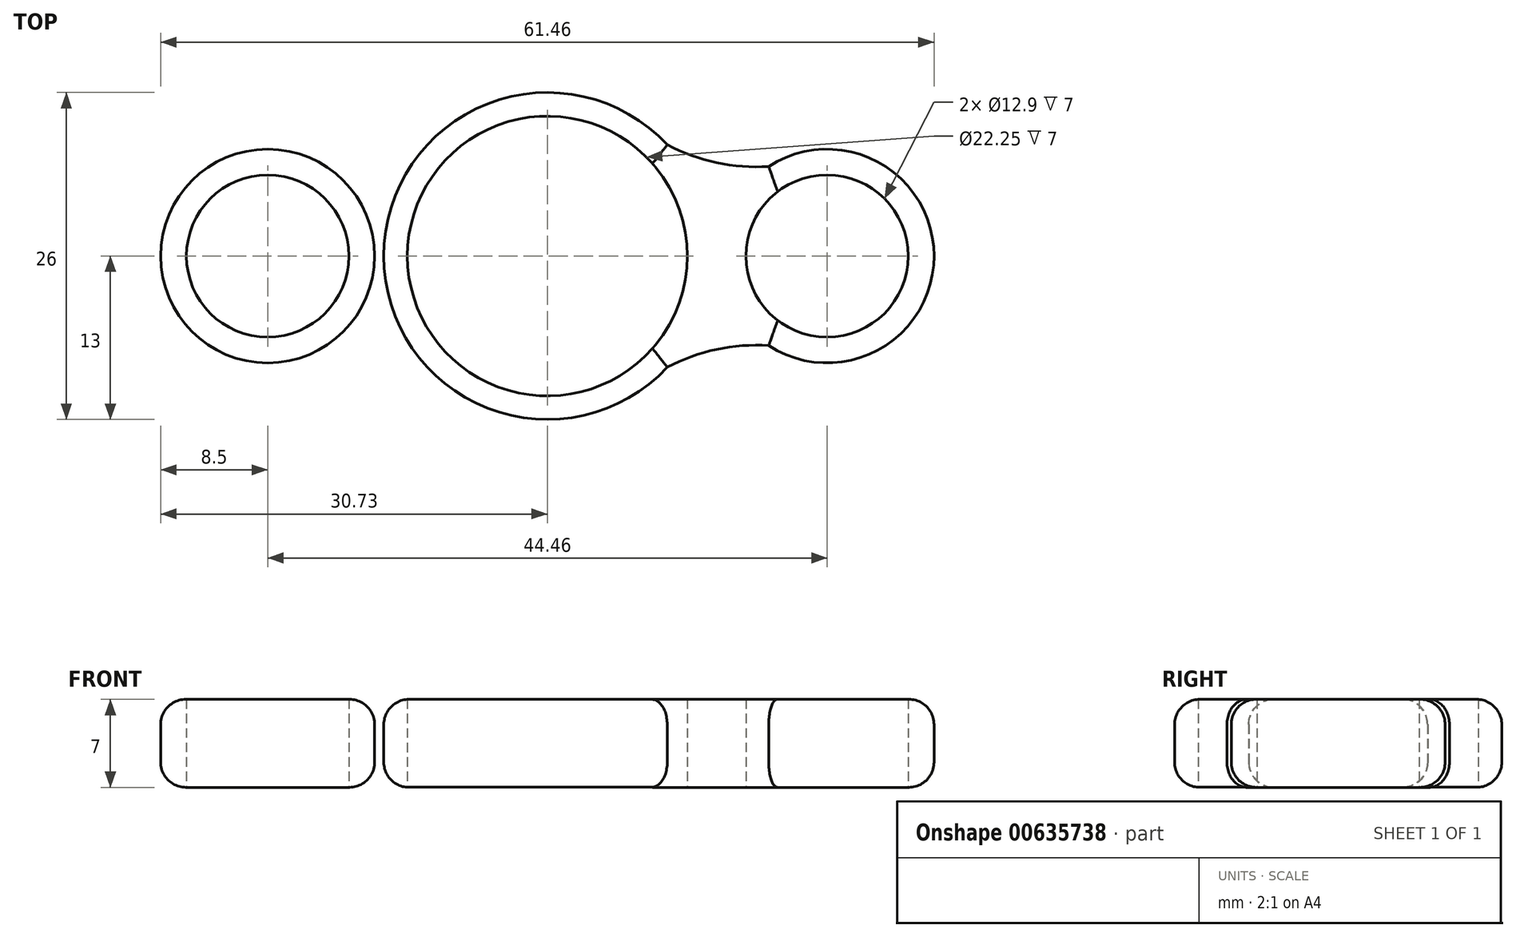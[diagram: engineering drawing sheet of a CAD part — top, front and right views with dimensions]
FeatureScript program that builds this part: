
annotation { "Feature Type Name" : "Feature", "Feature Type Description" : "" }
export const myFeature = defineFeature(function(context is Context, id is Id, definition is map)
    precondition{}
    {
        {
            var Q0;
            Q0=qCreatedBy(makeId("Top.planeOp"),FACE);
            var sketch = newSketch(context, id + "F0", { "sketchPlane" : qUnion([Q0])});
            skCircle(sketch, "E0", {"center": v(0, 0) * mm, "radius": 11.12 * mm});
            skLineSegment(sketch, "E1", {"start": v(0, 0) * mm, "end": v(30, 0) * mm, "construction": true});
            skCircle(sketch, "E2", {"center": v(22.23, 0) * mm, "radius": 6.45 * mm});
            skCircle(sketch, "E3", {"center": v(22.23, 0) * mm, "radius": 8.5 * mm});
            skCircle(sketch, "E4", {"center": v(0, 0) * mm, "radius": 13 * mm});
            skArc(sketch, "E5", {"start": v(17.6, -7.12) * mm, "mid": v(13.44, -7.42) * mm, "end": v(9.53, -8.84) * mm});
            skArc(sketch, "E6.MirrorCS", {"start": v(17.6, 7.12) * mm, "mid": v(13.44, 7.42) * mm, "end": v(9.53, 8.84) * mm});
            skLineSegment(sketch, "E7.1.4", {"start": v(-2.34, 0) * mm, "end": v(-32.34, 0) * mm, "construction": true});
            skPoint(sketch, "E7.center", {"position": v(-1.17, 0) * mm});
            skCircle(sketch, "E8.1.0", {"center": v(-22.23, 0) * mm, "radius": 6.45 * mm});
            skArc(sketch, "E8.1.1", {"start": v(-17.6, -7.12) * mm, "mid": v(-13.44, -7.42) * mm, "end": v(-9.53, -8.84) * mm});
            skCircle(sketch, "E8.1.2", {"center": v(-22.23, 0) * mm, "radius": 8.5 * mm});
            skArc(sketch, "E8.1.3", {"start": v(-17.6, 7.12) * mm, "mid": v(-13.44, 7.42) * mm, "end": v(-9.53, 8.84) * mm});
            skLineSegment(sketch, "E8.1.4", {"start": v(0, 0) * mm, "end": v(-30, 0) * mm, "construction": true});
            skSolve(sketch);
        }
        {
            var Q0;
            Q0=makeQuery(id+"F0.imprint","IMPRINT",FACE,{"disambiguationData":[TD([[makeQuery(id+"F0.imprint","IMPRINT",EDGE,{"derivedFrom":sQuery(id+"F0.wireOp",EDGE,"E2")}),-1.0]])]});
            var Q1;
            {var subQ0=sQuery(id+"F0.wireOp",EDGE,"E5");Q1=makeQuery(id+"F0.imprint","IMPRINT",FACE,{"disambiguationData":[TD([[makeQuery(id+"F0.imprint","IMPRINT",EDGE,{"derivedFrom":subQ0}),-1.0]])]});}
            var Q2;
            {var subQ0=sQuery(id+"F0.wireOp",EDGE,"E7.1.0");Q2=makeQuery(id+"F0.imprint","IMPRINT",FACE,{"disambiguationData":[TD([[makeQuery(id+"F0.imprint","IMPRINT",EDGE,{"derivedFrom":subQ0}),1.0]])]});}
            var Q3;
            Q3=makeQuery(id+"F0.imprint","IMPRINT",FACE,{"disambiguationData":[TD([[makeQuery(id+"F0.imprint","IMPRINT",EDGE,{"derivedFrom":sQuery(id+"F0.wireOp",EDGE,"E7.1.3")}),-1.0]])]});
            var Q4;
            Q4=makeQuery(id+"F0.imprint","IMPRINT",FACE,{"disambiguationData":[TD([[makeQuery(id+"F0.imprint","IMPRINT",EDGE,{"derivedFrom":sQuery(id+"F0.wireOp",EDGE,"E0")}),-1.0]])]});
            var Q5;
            Q5=makeQuery(id+"F0.imprint","IMPRINT",FACE,{"disambiguationData":[TD([[makeQuery(id+"F0.imprint","IMPRINT",EDGE,{"derivedFrom":sQuery(id+"F0.wireOp",EDGE,"E8.1.0")}),-1.0]])]});
            var Q6;
            {var subQ0=sQuery(id+"F0.wireOp",EDGE,"E8.1.1");Q6=makeQuery(id+"F0.imprint","IMPRINT",FACE,{"disambiguationData":[TD([[makeQuery(id+"F0.imprint","IMPRINT",EDGE,{"derivedFrom":subQ0}),1.0]])]});}
            extrude(context, id + "F1", {"entities" : qUnion([Q0, Q1, Q2, Q3, Q4, Q5, Q6]), "depth" : 7 * mm, "offsetDistance" : 25 * mm});
        }
        {
            var Q0;
            Q0=makeQuery(id+"F1.opExtrude","CAP_EDGE",EDGE,{"disambiguationData":[OSD([sQuery(id+"F0.wireOp",EDGE,"E8.1.1")])],"isStart":false});
            var Q1;
            {var subQ0=sQuery(id+"F0.wireOp",EDGE,"E4");Q1=makeQuery(id+"F1.opExtrude","CAP_EDGE",EDGE,{"disambiguationData":[OSD([subQ0]),TDD([makeQuery(id+"F0.imprint","IMPRINT",EDGE,{"disambiguationData":[TD([[makeQuery(id+"F0.imprint","INTERSECT",VERTEX,{"derivedFrom":[subQ0,sQuery(id+"F0.wireOp",EDGE,"E5")]}),1.0]])],"derivedFrom":subQ0})])],"isStart":false});}
            var Q2;
            Q2=makeQuery(id+"F1.opExtrude","CAP_EDGE",EDGE,{"disambiguationData":[OSD([sQuery(id+"F0.wireOp",EDGE,"E5")])],"isStart":false});
            var Q3;
            Q3=makeQuery(id+"F1.opExtrude","CAP_EDGE",EDGE,{"disambiguationData":[OSD([sQuery(id+"F0.wireOp",EDGE,"E3")])],"isStart":false});
            var Q4;
            Q4=makeQuery(id+"F1.opExtrude","CAP_EDGE",EDGE,{"disambiguationData":[OSD([sQuery(id+"F0.wireOp",EDGE,"E6.MirrorCS")])],"isStart":false});
            var Q5;
            {var subQ0=sQuery(id+"F0.wireOp",EDGE,"E4");Q5=makeQuery(id+"F1.opExtrude","CAP_EDGE",EDGE,{"disambiguationData":[OSD([subQ0]),TDD([makeQuery(id+"F0.imprint","IMPRINT",EDGE,{"disambiguationData":[TD([[makeQuery(id+"F0.imprint","INTERSECT",VERTEX,{"derivedFrom":[subQ0,sQuery(id+"F0.wireOp",EDGE,"E6.MirrorCS")]}),-1.0]])],"derivedFrom":subQ0})])],"isStart":false});}
            var Q6;
            Q6=makeQuery(id+"F1.opExtrude","CAP_EDGE",EDGE,{"disambiguationData":[OSD([sQuery(id+"F0.wireOp",EDGE,"E8.1.3")])],"isStart":false});
            var Q7;
            Q7=makeQuery(id+"F1.opExtrude","CAP_EDGE",EDGE,{"disambiguationData":[OSD([sQuery(id+"F0.wireOp",EDGE,"E8.1.2")])],"isStart":false});
            var Q8;
            Q8=makeQuery(id+"F1.opExtrude","CAP_EDGE",EDGE,{"disambiguationData":[OSD([sQuery(id+"F0.wireOp",EDGE,"E8.1.2")])],"isStart":true});
            var Q9;
            Q9=makeQuery(id+"F1.opExtrude","CAP_EDGE",EDGE,{"disambiguationData":[OSD([sQuery(id+"F0.wireOp",EDGE,"E8.1.3")])],"isStart":true});
            var Q10;
            {var subQ0=sQuery(id+"F0.wireOp",EDGE,"E4");Q10=makeQuery(id+"F1.opExtrude","CAP_EDGE",EDGE,{"disambiguationData":[OSD([subQ0]),TDD([makeQuery(id+"F0.imprint","IMPRINT",EDGE,{"disambiguationData":[TD([[makeQuery(id+"F0.imprint","INTERSECT",VERTEX,{"derivedFrom":[subQ0,sQuery(id+"F0.wireOp",EDGE,"E6.MirrorCS")]}),-1.0]])],"derivedFrom":subQ0})])],"isStart":true});}
            var Q11;
            Q11=makeQuery(id+"F1.opExtrude","CAP_EDGE",EDGE,{"disambiguationData":[OSD([sQuery(id+"F0.wireOp",EDGE,"E6.MirrorCS")])],"isStart":true});
            var Q12;
            Q12=makeQuery(id+"F1.opExtrude","CAP_EDGE",EDGE,{"disambiguationData":[OSD([sQuery(id+"F0.wireOp",EDGE,"E3")])],"isStart":true});
            var Q13;
            Q13=makeQuery(id+"F1.opExtrude","CAP_EDGE",EDGE,{"disambiguationData":[OSD([sQuery(id+"F0.wireOp",EDGE,"E5")])],"isStart":true});
            var Q14;
            {var subQ0=sQuery(id+"F0.wireOp",EDGE,"E4");Q14=makeQuery(id+"F1.opExtrude","CAP_EDGE",EDGE,{"disambiguationData":[OSD([subQ0]),TDD([makeQuery(id+"F0.imprint","IMPRINT",EDGE,{"disambiguationData":[TD([[makeQuery(id+"F0.imprint","INTERSECT",VERTEX,{"derivedFrom":[subQ0,sQuery(id+"F0.wireOp",EDGE,"E5")]}),1.0]])],"derivedFrom":subQ0})])],"isStart":true});}
            var Q15;
            Q15=makeQuery(id+"F1.opExtrude","CAP_EDGE",EDGE,{"disambiguationData":[OSD([sQuery(id+"F0.wireOp",EDGE,"E8.1.1")])],"isStart":true});
            fillet(context, id + "F2", {"entities" : qUnion([Q0, Q1, Q2, Q3, Q4, Q5, Q6, Q7, Q8, Q9, Q10, Q11, Q12, Q13, Q14, Q15]), "radius" : 2 * mm, "tangentPropagation" : true, "allowEdgeOverflow" : false});
        }
    });
